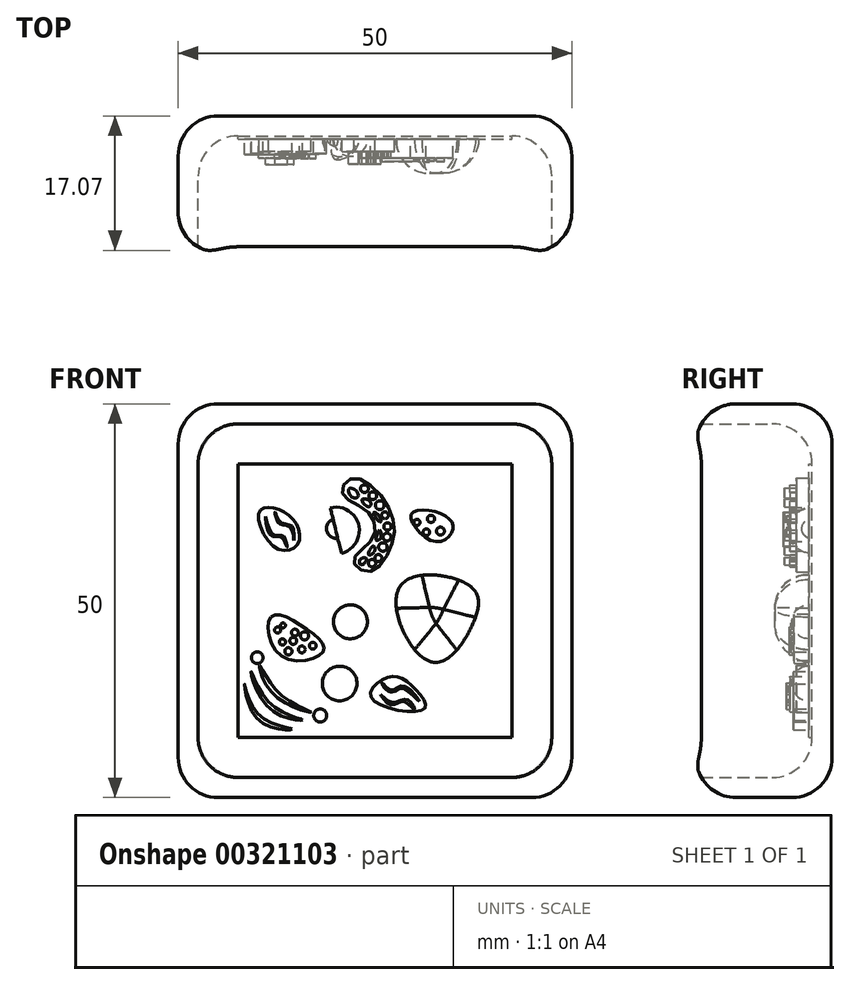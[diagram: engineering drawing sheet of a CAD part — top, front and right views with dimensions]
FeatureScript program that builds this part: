
annotation { "Feature Type Name" : "Feature", "Feature Type Description" : "" }
export const myFeature = defineFeature(function(context is Context, id is Id, definition is map)
    precondition{}
    {
        {
            var Q0;
            Q0=qCreatedBy(makeId("Front.planeOp"),FACE);
            var sketch = newSketch(context, id + "F0", { "sketchPlane" : qUnion([Q0])});
            skLineSegment(sketch, "E0.bottom", {"start": v(0, 0) * mm, "end": v(50, 0) * mm});
            skLineSegment(sketch, "E0.top", {"start": v(0, 50) * mm, "end": v(50, 50) * mm});
            skLineSegment(sketch, "E0.left", {"start": v(0, 0) * mm, "end": v(0, 50) * mm});
            skLineSegment(sketch, "E0.right", {"start": v(50, 0) * mm, "end": v(50, 50) * mm});
            skSolve(sketch);
        }
        {
            var Q0;
            Q0=makeQuery(id+"F0.imprint","IMPRINT",FACE,{"disambiguationData":[TD([[makeQuery(id+"F0.imprint","IMPRINT",EDGE,{"derivedFrom":sQuery(id+"F0.wireOp",EDGE,"E0.bottom")}),1.0]])]});
            var sketch = newSketch(context, id + "F1", { "sketchPlane" : qUnion([Q0])});
            skSolve(sketch);
        }
        {
            var Q0;
            Q0=makeQuery(id+"F1.imprint","IMPRINT",FACE,{"disambiguationData":[TD([[makeQuery(id+"F1.imprint","IMPRINT",EDGE,{"derivedFrom":makeQuery(id+"F0.imprint","IMPRINT",EDGE,{"derivedFrom":sQuery(id+"F0.wireOp",EDGE,"E0.bottom")})}),1.0]])]});
            extrude(context, id + "F2", {"entities" : qUnion([Q0]), "depth" : 17.3 * mm});
        }
        {
            var Q0;
            Q0=makeQuery(id+"F2.opExtrude","CAP_FACE",FACE,{"disambiguationData":[OSD([sQuery(id+"F0.wireOp",EDGE,"E0.bottom"),sQuery(id+"F0.wireOp",EDGE,"E0.top"),sQuery(id+"F0.wireOp",EDGE,"E0.left"),sQuery(id+"F0.wireOp",EDGE,"E0.right")])],"isStart":false});
            shell(context, id + "F3", {"entities" : qUnion([Q0]), "thickness" : 2.54 * mm});
        }
        {
            var Q0;
            Q0=makeQuery(id+"F3.opShell","OFFSET_FACE",FACE,{"disambiguationData":[OSD([sQuery(id+"F0.wireOp",EDGE,"E0.bottom"),sQuery(id+"F0.wireOp",EDGE,"E0.top"),sQuery(id+"F0.wireOp",EDGE,"E0.left"),sQuery(id+"F0.wireOp",EDGE,"E0.right")])]});
            var Q1;
            Q1=makeQuery(id+"F2.opExtrude","SWEPT_EDGE",EDGE,{"disambiguationData":[OSD([sQuery(id+"F0.wireOp",EDGE,"E0.top"),sQuery(id+"F0.wireOp",EDGE,"E0.right")])]});
            var Q2;
            Q2=makeQuery(id+"F2.opExtrude","SWEPT_EDGE",EDGE,{"disambiguationData":[OSD([sQuery(id+"F0.wireOp",EDGE,"E0.top"),sQuery(id+"F0.wireOp",EDGE,"E0.left")])]});
            var Q3;
            Q3=makeQuery(id+"F2.opExtrude","SWEPT_EDGE",EDGE,{"disambiguationData":[OSD([sQuery(id+"F0.wireOp",EDGE,"E0.bottom"),sQuery(id+"F0.wireOp",EDGE,"E0.left")])]});
            var Q4;
            Q4=makeQuery(id+"F2.opExtrude","SWEPT_EDGE",EDGE,{"disambiguationData":[OSD([sQuery(id+"F0.wireOp",EDGE,"E0.bottom"),sQuery(id+"F0.wireOp",EDGE,"E0.right")])]});
            var Q5;
            Q5=makeQuery(id+"F2.opExtrude","CAP_EDGE",EDGE,{"disambiguationData":[OSD([sQuery(id+"F0.wireOp",EDGE,"E0.top")])],"isStart":true});
            var Q6;
            Q6=makeQuery(id+"F2.opExtrude","CAP_EDGE",EDGE,{"disambiguationData":[OSD([sQuery(id+"F0.wireOp",EDGE,"E0.bottom")])],"isStart":true});
            var Q7;
            Q7=makeQuery(id+"F3.opShell","OFFSET_EDGE",EDGE,{"disambiguationData":[OSD([sQuery(id+"F0.wireOp",EDGE,"E0.top"),sQuery(id+"F0.wireOp",EDGE,"E0.right")])]});
            var Q8;
            Q8=makeQuery(id+"F3.opShell","OFFSET_EDGE",EDGE,{"disambiguationData":[OSD([sQuery(id+"F0.wireOp",EDGE,"E0.bottom"),sQuery(id+"F0.wireOp",EDGE,"E0.right")])]});
            var Q9;
            Q9=makeQuery(id+"F3.opShell","OFFSET_EDGE",EDGE,{"disambiguationData":[OSD([sQuery(id+"F0.wireOp",EDGE,"E0.bottom"),sQuery(id+"F0.wireOp",EDGE,"E0.left")])]});
            var Q10;
            Q10=makeQuery(id+"F3.opShell","OFFSET_EDGE",EDGE,{"disambiguationData":[OSD([sQuery(id+"F0.wireOp",EDGE,"E0.top"),sQuery(id+"F0.wireOp",EDGE,"E0.left")])]});
            fillet(context, id + "F4", {"entities" : qUnion([Q0, Q1, Q2, Q3, Q4, Q5, Q6, Q7, Q8, Q9, Q10]), "radius" : 5.08 * mm, "tangentPropagation" : true, "allowEdgeOverflow" : false});
        }
        {
            var Q0;
            Q0=makeQuery(id+"F3.opShell","OFFSET_FACE",FACE,{"disambiguationData":[OSD([sQuery(id+"F0.wireOp",EDGE,"E0.bottom"),sQuery(id+"F0.wireOp",EDGE,"E0.top"),sQuery(id+"F0.wireOp",EDGE,"E0.left"),sQuery(id+"F0.wireOp",EDGE,"E0.right")])]});
            var Q1;
            Q1=makeQuery(id+"F2.opExtrude","CAP_EDGE",EDGE,{"disambiguationData":[OSD([sQuery(id+"F0.wireOp",EDGE,"E0.left")])],"isStart":true});
            var Q2;
            Q2=makeQuery(id+"F2.opExtrude","CAP_EDGE",EDGE,{"disambiguationData":[OSD([sQuery(id+"F0.wireOp",EDGE,"E0.right")])],"isStart":true});
            fillet(context, id + "F5", {"entities" : qUnion([Q0, Q1, Q2]), "radius" : 5.08 * mm, "tangentPropagation" : true, "allowEdgeOverflow" : false});
        }
        {
            var Q0;
            Q0=makeQuery(id+"F2.opExtrude","CAP_EDGE",EDGE,{"disambiguationData":[OSD([sQuery(id+"F0.wireOp",EDGE,"E0.right")])],"isStart":false});
            fillet(context, id + "F6", {"entities" : qUnion([Q0]), "radius" : 5.08 * mm, "tangentPropagation" : true, "allowEdgeOverflow" : false});
        }
        {
            var Q0;
            Q0=makeQuery(id+"F3.opShell","OFFSET_FACE",FACE,{"disambiguationData":[OSD([sQuery(id+"F0.wireOp",EDGE,"E0.bottom"),sQuery(id+"F0.wireOp",EDGE,"E0.top"),sQuery(id+"F0.wireOp",EDGE,"E0.left"),sQuery(id+"F0.wireOp",EDGE,"E0.right")])]});
            var sketch = newSketch(context, id + "F7", { "sketchPlane" : qUnion([Q0])});
            skLineSegment(sketch, "E1", {"start": v(20.1, 35.5) * mm, "end": v(20.1, 32.84) * mm});
            skArc(sketch, "E2", {"start": v(20.1, 32.84) * mm, "mid": v(21.4, 34.17) * mm, "end": v(20.1, 35.5) * mm});
            skSolve(sketch);
        }
        {
            var Q0;
            Q0=makeQuery(id+"F7.imprint","IMPRINT",FACE,{"disambiguationData":[TD([[makeQuery(id+"F7.imprint","IMPRINT",EDGE,{"derivedFrom":sQuery(id+"F7.wireOp",EDGE,"E1")}),1.0]])]});
            var Q1;
            Q1=sQuery(id+"F7.wireOp",EDGE,"E1");
            revolve(context, id + "F8", {"entities" : qUnion([Q0]), "axis" : qUnion([Q1]), "revolveType" : RevolveType.ONE_DIRECTION, "angle" : 180 * degree});
        }
        {
            var Q0;
            Q0=makeQuery(id+"F3.opShell","OFFSET_FACE",FACE,{"disambiguationData":[OSD([sQuery(id+"F0.wireOp",EDGE,"E0.bottom"),sQuery(id+"F0.wireOp",EDGE,"E0.top"),sQuery(id+"F0.wireOp",EDGE,"E0.left"),sQuery(id+"F0.wireOp",EDGE,"E0.right")])]});
            var sketch = newSketch(context, id + "F9", { "sketchPlane" : qUnion([Q0])});
            skLineSegment(sketch, "E3", {"start": v(19.32, 36.82) * mm, "end": v(20.75, 31) * mm});
            skArc(sketch, "E4", {"start": v(20.75, 31) * mm, "mid": v(22.96, 34.64) * mm, "end": v(19.32, 36.82) * mm});
            skSolve(sketch);
        }
        {
            var Q0;
            Q0=makeQuery(id+"F9.imprint","IMPRINT",FACE,{"disambiguationData":[TD([[makeQuery(id+"F9.imprint","IMPRINT",EDGE,{"derivedFrom":sQuery(id+"F9.wireOp",EDGE,"E3")}),1.0]])]});
            var Q1;
            Q1=sQuery(id+"F9.wireOp",EDGE,"E3");
            revolve(context, id + "F10", {"entities" : qUnion([Q0]), "axis" : qUnion([Q1]), "revolveType" : RevolveType.ONE_DIRECTION, "angle" : 90 * degree});
        }
        {
            var Q0;
            Q0=makeQuery(id+"F3.opShell","OFFSET_FACE",FACE,{"disambiguationData":[OSD([sQuery(id+"F0.wireOp",EDGE,"E0.bottom"),sQuery(id+"F0.wireOp",EDGE,"E0.top"),sQuery(id+"F0.wireOp",EDGE,"E0.left"),sQuery(id+"F0.wireOp",EDGE,"E0.right")])]});
            var sketch = newSketch(context, id + "F11", { "sketchPlane" : qUnion([Q0])});
            skFitSpline(sketch, "E5", {"points": [v(37, 26.9) * mm, v(37.56, 22.37) * mm, v(32.09, 17.25) * mm, v(28.13, 26.72) * mm, v(37, 26.9) * mm]});
            skSolve(sketch);
        }
        {
            var Q0;
            Q0=makeQuery(id+"F11.imprint","IMPRINT",FACE,{"disambiguationData":[TD([[makeQuery(id+"F11.imprint","IMPRINT",EDGE,{"derivedFrom":sQuery(id+"F11.wireOp",EDGE,"E5")}),-1.0]])]});
            extrude(context, id + "F12", {"entities" : qUnion([Q0]), "depth" : 4.73 * mm});
        }
        {
            var Q0;
            Q0=makeQuery(id+"F3.opShell","OFFSET_FACE",FACE,{"disambiguationData":[OSD([sQuery(id+"F0.wireOp",EDGE,"E0.bottom"),sQuery(id+"F0.wireOp",EDGE,"E0.top"),sQuery(id+"F0.wireOp",EDGE,"E0.left"),sQuery(id+"F0.wireOp",EDGE,"E0.right")])]});
            var sketch = newSketch(context, id + "F13", { "sketchPlane" : qUnion([Q0])});
            skFitSpline(sketch, "E6", {"points": [v(11.8, 22.95) * mm, v(16.02, 21.6) * mm, v(18.48, 18.58) * mm, v(13.15, 17.95) * mm, v(11.8, 22.95) * mm]});
            skSolve(sketch);
        }
        {
            var Q0;
            Q0 = qSketchRegion(id + "F13", true);
            extrude(context, id + "F14", {"entities" : qUnion([Q0]), "operationType" : NewBodyOperationType.ADD, "depth" : 2.28 * mm});
        }
        {
            var Q0;
            Q0=makeQuery(id+"F14.opExtrude","CAP_FACE",FACE,{"disambiguationData":[OSD([sQuery(id+"F13.wireOp",EDGE,"E6")])],"isStart":false});
            var sketch = newSketch(context, id + "F15", { "sketchPlane" : qUnion([Q0])});
            skCircle(sketch, "E7", {"center": v(15.71, 18.8) * mm, "radius": 0.44 * mm});
            skSolve(sketch);
        }
        {
            var Q0;
            Q0 = qSketchRegion(id + "F15", true);
            extrude(context, id + "F16", {"entities" : qUnion([Q0]), "operationType" : NewBodyOperationType.ADD, "depth" : 0.35 * mm});
        }
        {
            var Q0;
            Q0=makeQuery(id+"F14.opExtrude","CAP_FACE",FACE,{"disambiguationData":[OSD([sQuery(id+"F13.wireOp",EDGE,"E6")])],"isStart":false});
            var sketch = newSketch(context, id + "F17", { "sketchPlane" : qUnion([Q0])});
            skCircle(sketch, "E8", {"center": v(13.24, 19.75) * mm, "radius": 0.4 * mm});
            skSolve(sketch);
        }
        {
            var Q0;
            Q0 = qSketchRegion(id + "F17", true);
            extrude(context, id + "F18", {"entities" : qUnion([Q0]), "operationType" : NewBodyOperationType.ADD, "depth" : 0.35 * mm});
        }
        {
            var Q0;
            Q0=makeQuery(id+"F14.opExtrude","CAP_FACE",FACE,{"disambiguationData":[OSD([sQuery(id+"F13.wireOp",EDGE,"E6")])],"isStart":false});
            var sketch = newSketch(context, id + "F19", { "sketchPlane" : qUnion([Q0])});
            skCircle(sketch, "E9", {"center": v(13.32, 21.86) * mm, "radius": 0.3 * mm});
            skSolve(sketch);
        }
        {
            var Q0;
            Q0 = qSketchRegion(id + "F19", true);
            extrude(context, id + "F20", {"entities" : qUnion([Q0]), "operationType" : NewBodyOperationType.ADD, "depth" : 0.39 * mm});
        }
        {
            var Q0;
            Q0=makeQuery(id+"F14.opExtrude","CAP_FACE",FACE,{"disambiguationData":[OSD([sQuery(id+"F13.wireOp",EDGE,"E6")])],"isStart":false});
            var sketch = newSketch(context, id + "F21", { "sketchPlane" : qUnion([Q0])});
            skCircle(sketch, "E10", {"center": v(14.84, 20.95) * mm, "radius": 0.43 * mm});
            skSolve(sketch);
        }
        {
            var Q0;
            Q0 = qSketchRegion(id + "F21", true);
            var Q1;
            Q1=makeQuery(id+"F3.opShell","OFFSET_FACE",FACE,{"disambiguationData":[OSD([sQuery(id+"F0.wireOp",EDGE,"E0.bottom"),sQuery(id+"F0.wireOp",EDGE,"E0.top"),sQuery(id+"F0.wireOp",EDGE,"E0.left"),sQuery(id+"F0.wireOp",EDGE,"E0.right")])]});
            extrude(context, id + "F22", {"entities" : qUnion([Q0, Q1]), "operationType" : NewBodyOperationType.ADD, "depth" : 0.4 * mm});
        }
        {
            var Q0;
            Q0=makeQuery(id+"F14.opExtrude","CAP_FACE",FACE,{"disambiguationData":[OSD([sQuery(id+"F13.wireOp",EDGE,"E6")])],"isStart":false});
            var sketch = newSketch(context, id + "F23", { "sketchPlane" : qUnion([Q0])});
            skSolve(sketch);
        }
        {
            var Q0;
            Q0=makeQuery(id+"F23.imprint","IMPRINT",FACE,{"disambiguationData":[TD([[makeQuery(id+"F23.imprint","IMPRINT",EDGE,{"derivedFrom":makeQuery(id+"F14.opExtrude","CAP_EDGE",EDGE,{"disambiguationData":[OSD([sQuery(id+"F13.wireOp",EDGE,"E6")])],"isStart":false})}),-1.0]])]});
            var sketch = newSketch(context, id + "F24", { "sketchPlane" : qUnion([Q0])});
            skSolve(sketch);
        }
        {
            var Q0;
            Q0=makeQuery(id+"F22.opExtrude","CAP_FACE",FACE,{"disambiguationData":[OSD([sQuery(id+"F0.wireOp",EDGE,"E0.bottom"),sQuery(id+"F0.wireOp",EDGE,"E0.top"),sQuery(id+"F0.wireOp",EDGE,"E0.left"),sQuery(id+"F0.wireOp",EDGE,"E0.right")])],"isStart":false});
            var sketch = newSketch(context, id + "F25", { "sketchPlane" : qUnion([Q0])});
            skFitSpline(sketch, "E11", {"points": [v(29.59, 35.96) * mm, v(33.47, 36.03) * mm, v(34.91, 34.05) * mm, v(32.52, 32.54) * mm, v(29.59, 35.96) * mm]});
            skSolve(sketch);
        }
        {
            var Q0;
            Q0 = qSketchRegion(id + "F25", true);
            extrude(context, id + "F26", {"entities" : qUnion([Q0]), "operationType" : NewBodyOperationType.ADD, "depth" : 2.37 * mm});
        }
        {
            var Q0;
            Q0=makeQuery(id+"F26.opExtrude","CAP_FACE",FACE,{"disambiguationData":[OSD([sQuery(id+"F25.wireOp",EDGE,"E11")])],"isStart":false});
            var sketch = newSketch(context, id + "F27", { "sketchPlane" : qUnion([Q0])});
            skCircle(sketch, "E12", {"center": v(33.32, 33.84) * mm, "radius": 0.5 * mm});
            skSolve(sketch);
        }
        {
            var Q0;
            Q0 = qSketchRegion(id + "F27", true);
            extrude(context, id + "F28", {"entities" : qUnion([Q0]), "operationType" : NewBodyOperationType.ADD, "depth" : 0.45 * mm});
        }
        {
            var Q0;
            Q0=makeQuery(id+"F26.opExtrude","CAP_FACE",FACE,{"disambiguationData":[OSD([sQuery(id+"F25.wireOp",EDGE,"E11")])],"isStart":false});
            var sketch = newSketch(context, id + "F29", { "sketchPlane" : qUnion([Q0])});
            skCircle(sketch, "E13", {"center": v(32.12, 35.4) * mm, "radius": 0.46 * mm});
            skSolve(sketch);
        }
        {
            var Q0;
            Q0 = qSketchRegion(id + "F29", true);
            extrude(context, id + "F30", {"entities" : qUnion([Q0]), "operationType" : NewBodyOperationType.ADD, "depth" : 0.42 * mm});
        }
        {
            var Q0;
            Q0=makeQuery(id+"F26.opExtrude","CAP_FACE",FACE,{"disambiguationData":[OSD([sQuery(id+"F25.wireOp",EDGE,"E11")])],"isStart":false});
            var sketch = newSketch(context, id + "F31", { "sketchPlane" : qUnion([Q0])});
            skCircle(sketch, "E14", {"center": v(30.33, 34.94) * mm, "radius": 0.4 * mm});
            skSolve(sketch);
        }
        {
            var Q0;
            Q0 = qSketchRegion(id + "F31", true);
            extrude(context, id + "F32", {"entities" : qUnion([Q0]), "operationType" : NewBodyOperationType.ADD, "depth" : 0.3 * mm});
        }
        {
            var Q0;
            Q0=makeQuery(id+"F22.opExtrude","CAP_FACE",FACE,{"disambiguationData":[OSD([sQuery(id+"F0.wireOp",EDGE,"E0.bottom"),sQuery(id+"F0.wireOp",EDGE,"E0.top"),sQuery(id+"F0.wireOp",EDGE,"E0.left"),sQuery(id+"F0.wireOp",EDGE,"E0.right")])],"isStart":false});
            var sketch = newSketch(context, id + "F33", { "sketchPlane" : qUnion([Q0])});
            skFitSpline(sketch, "E15", {"points": [v(26.58, 15.26) * mm, v(29.8, 14.11) * mm, v(31.24, 11.22) * mm, v(24.55, 12.68) * mm, v(26.58, 15.26) * mm]});
            skFitSpline(sketch, "E16", {"points": [v(12.15, 36.78) * mm, v(14.97, 34.86) * mm, v(15.1, 32.04) * mm, v(12.4, 31.72) * mm, v(10.26, 36.2) * mm, v(12.15, 36.78) * mm]});
            skSolve(sketch);
        }
        {
            var Q0;
            Q0=makeQuery(id+"F33.imprint","IMPRINT",FACE,{"disambiguationData":[TD([[makeQuery(id+"F33.imprint","IMPRINT",EDGE,{"derivedFrom":sQuery(id+"F33.wireOp",EDGE,"E16")}),-1.0]])]});
            var Q1;
            Q1=makeQuery(id+"F33.imprint","IMPRINT",FACE,{"disambiguationData":[TD([[makeQuery(id+"F33.imprint","IMPRINT",EDGE,{"derivedFrom":sQuery(id+"F33.wireOp",EDGE,"E15")}),-1.0]])]});
            extrude(context, id + "F34", {"entities" : qUnion([Q0, Q1]), "depth" : 2.38 * mm});
        }
        {
            var Q0;
            Q0=makeQuery(id+"F34.opExtrude","CAP_FACE",FACE,{"disambiguationData":[OSD([sQuery(id+"F33.wireOp",EDGE,"E15")])],"isStart":false});
            var sketch = newSketch(context, id + "F35", { "sketchPlane" : qUnion([Q0])});
            skFitSpline(sketch, "E17", {"points": [v(30.65, 12.2) * mm, v(28.67, 14.17) * mm, v(27.02, 13.66) * mm, v(25.92, 14.56) * mm, v(26.32, 13.81) * mm, v(27.45, 13.44) * mm, v(28.5, 13.88) * mm, v(30.65, 12.2) * mm]});
            skFitSpline(sketch, "E18", {"points": [v(25.7, 13.08) * mm, v(26.97, 11.8) * mm, v(28.71, 12.19) * mm, v(30.03, 11.17) * mm, v(29.21, 12.42) * mm, v(27.06, 12.12) * mm, v(25.7, 13.08) * mm]});
            skSolve(sketch);
        }
        {
            var Q0;
            Q0 = qSketchRegion(id + "F35", true);
            extrude(context, id + "F36", {"entities" : qUnion([Q0]), "operationType" : NewBodyOperationType.ADD, "depth" : 0.47 * mm});
        }
        {
            var Q0;
            Q0=makeQuery(id+"F34.opExtrude","CAP_FACE",FACE,{"disambiguationData":[OSD([sQuery(id+"F33.wireOp",EDGE,"E16")])],"isStart":false});
            var sketch = newSketch(context, id + "F37", { "sketchPlane" : qUnion([Q0])});
            skFitSpline(sketch, "E19", {"points": [v(11.11, 35.7) * mm, v(11.7, 33.36) * mm, v(13.12, 33.05) * mm, v(13.86, 31.8) * mm, v(13.7, 32.52) * mm, v(13.2, 33.24) * mm, v(11.88, 33.6) * mm, v(11.11, 35.7) * mm]});
            skFitSpline(sketch, "E20", {"points": [v(14.7, 32.66) * mm, v(14.53, 34.36) * mm, v(13.05, 34.95) * mm, v(12.3, 36.27) * mm, v(12.46, 35.51) * mm, v(12.91, 34.73) * mm, v(14.35, 34.18) * mm, v(14.7, 32.66) * mm]});
            skSolve(sketch);
        }
        {
            var Q0;
            Q0 = qSketchRegion(id + "F37", true);
            extrude(context, id + "F38", {"entities" : qUnion([Q0]), "operationType" : NewBodyOperationType.ADD, "depth" : 0.87 * mm});
        }
        {
            var Q0;
            Q0=makeQuery(id+"F12.opExtrude","CAP_EDGE",EDGE,{"disambiguationData":[OSD([sQuery(id+"F11.wireOp",EDGE,"E5")])],"isStart":false});
            fillet(context, id + "F39", {"entities" : qUnion([Q0]), "radius" : 4.14 * mm, "tangentPropagation" : true, "allowEdgeOverflow" : false});
        }
        {
            var Q0;
            Q0=makeQuery(id+"F22.opExtrude","CAP_FACE",FACE,{"disambiguationData":[OSD([sQuery(id+"F0.wireOp",EDGE,"E0.bottom"),sQuery(id+"F0.wireOp",EDGE,"E0.top"),sQuery(id+"F0.wireOp",EDGE,"E0.left"),sQuery(id+"F0.wireOp",EDGE,"E0.right")])],"isStart":false});
            var sketch = newSketch(context, id + "F40", { "sketchPlane" : qUnion([Q0])});
            skLineSegment(sketch, "E21", {"start": v(23.9, 21.55) * mm, "end": v(19.88, 23.09) * mm});
            skArc(sketch, "E22", {"start": v(23.9, 21.55) * mm, "mid": v(22.66, 24.33) * mm, "end": v(19.88, 23.09) * mm});
            skSolve(sketch);
        }
        {
            var Q0;
            Q0=makeQuery(id+"F40.imprint","IMPRINT",FACE,{"disambiguationData":[TD([[makeQuery(id+"F40.imprint","IMPRINT",EDGE,{"derivedFrom":sQuery(id+"F40.wireOp",EDGE,"E21")}),-1.0]])]});
            var Q1;
            Q1=sQuery(id+"F40.wireOp",EDGE,"E21");
            revolve(context, id + "F41", {"entities" : qUnion([Q0]), "axis" : qUnion([Q1]), "revolveType" : RevolveType.ONE_DIRECTION, "oppositeDirection" : true, "angle" : 180 * degree});
        }
        {
            var Q0;
            Q0=makeQuery(id+"F22.opExtrude","CAP_FACE",FACE,{"disambiguationData":[OSD([sQuery(id+"F0.wireOp",EDGE,"E0.bottom"),sQuery(id+"F0.wireOp",EDGE,"E0.top"),sQuery(id+"F0.wireOp",EDGE,"E0.left"),sQuery(id+"F0.wireOp",EDGE,"E0.right")])],"isStart":false});
            var sketch = newSketch(context, id + "F42", { "sketchPlane" : qUnion([Q0])});
            skLineSegment(sketch, "E23", {"start": v(22.37, 15.7) * mm, "end": v(18.67, 13.25) * mm});
            skArc(sketch, "E24", {"start": v(18.67, 13.25) * mm, "mid": v(21.73, 12.65) * mm, "end": v(22.37, 15.7) * mm});
            skSolve(sketch);
        }
        {
            var Q0;
            Q0=makeQuery(id+"F42.imprint","IMPRINT",FACE,{"disambiguationData":[TD([[makeQuery(id+"F42.imprint","IMPRINT",EDGE,{"derivedFrom":sQuery(id+"F42.wireOp",EDGE,"E23")}),1.0]])]});
            var Q1;
            Q1=sQuery(id+"F42.wireOp",EDGE,"E23");
            revolve(context, id + "F43", {"entities" : qUnion([Q0]), "axis" : qUnion([Q1]), "revolveType" : RevolveType.ONE_DIRECTION, "angle" : 180 * degree});
        }
        {
            var Q0;
            Q0=makeQuery(id+"F22.opExtrude","CAP_FACE",FACE,{"disambiguationData":[OSD([sQuery(id+"F0.wireOp",EDGE,"E0.bottom"),sQuery(id+"F0.wireOp",EDGE,"E0.top"),sQuery(id+"F0.wireOp",EDGE,"E0.left"),sQuery(id+"F0.wireOp",EDGE,"E0.right")])],"isStart":false});
            var sketch = newSketch(context, id + "F44", { "sketchPlane" : qUnion([Q0])});
            skFitSpline(sketch, "E25", {"points": [v(10.33, 16.78) * mm, v(12.23, 13) * mm, v(16.88, 10.83) * mm, v(12.93, 13.17) * mm, v(10.33, 16.78) * mm]});
            skSolve(sketch);
        }
        {
            var Q0;
            Q0 = qSketchRegion(id + "F44", true);
            extrude(context, id + "F45", {"entities" : qUnion([Q0]), "depth" : 1.55 * mm});
        }
        {
            var Q0;
            Q0=makeQuery(id+"F22.opExtrude","CAP_FACE",FACE,{"disambiguationData":[OSD([sQuery(id+"F0.wireOp",EDGE,"E0.bottom"),sQuery(id+"F0.wireOp",EDGE,"E0.top"),sQuery(id+"F0.wireOp",EDGE,"E0.left"),sQuery(id+"F0.wireOp",EDGE,"E0.right")])],"isStart":false});
            var sketch = newSketch(context, id + "F46", { "sketchPlane" : qUnion([Q0])});
            skFitSpline(sketch, "E26", {"points": [v(15.8, 9.85) * mm, v(11.61, 11.28) * mm, v(9.24, 16.03) * mm, v(11.78, 11.87) * mm, v(15.8, 9.85) * mm]});
            skFitSpline(sketch, "E27", {"points": [v(14.47, 8.68) * mm, v(10.27, 9.8) * mm, v(8.43, 14.42) * mm, v(10.27, 10.5) * mm, v(14.47, 8.68) * mm]});
            skSolve(sketch);
        }
        {
            var Q0;
            Q0 = qSketchRegion(id + "F46", true);
            extrude(context, id + "F47", {"entities" : qUnion([Q0]), "depth" : 1.97 * mm});
        }
        {
            var Q0;
            Q0=makeQuery(id+"F22.opExtrude","CAP_FACE",FACE,{"disambiguationData":[OSD([sQuery(id+"F0.wireOp",EDGE,"E0.bottom"),sQuery(id+"F0.wireOp",EDGE,"E0.top"),sQuery(id+"F0.wireOp",EDGE,"E0.left"),sQuery(id+"F0.wireOp",EDGE,"E0.right")])],"isStart":false});
            var sketch = newSketch(context, id + "F48", { "sketchPlane" : qUnion([Q0])});
            skFitSpline(sketch, "E28", {"points": [v(20.88, 38.62) * mm, v(24.15, 36.24) * mm, v(24.65, 32.82) * mm, v(22.31, 30.13) * mm, v(24.14, 28.68) * mm, v(27.18, 32.2) * mm, v(26.47, 37.31) * mm, v(22.15, 40.56) * mm, v(20.88, 38.62) * mm]});
            skSolve(sketch);
        }
        {
            var Q0;
            Q0 = qSketchRegion(id + "F48", true);
            extrude(context, id + "F49", {"entities" : qUnion([Q0]), "depth" : 1.6 * mm});
        }
        {
            var Q0;
            Q0=makeQuery(id+"F49.opExtrude","CAP_FACE",FACE,{"disambiguationData":[OSD([sQuery(id+"F48.wireOp",EDGE,"E28")])],"isStart":false});
            var sketch = newSketch(context, id + "F50", { "sketchPlane" : qUnion([Q0])});
            skFitSpline(sketch, "E29", {"points": [v(21.7, 39.19) * mm, v(22.52, 39.05) * mm, v(22.85, 38.22) * mm, v(22.13, 38.13) * mm, v(21.7, 39.19) * mm]});
            skFitSpline(sketch, "E30", {"points": [v(23.39, 37.84) * mm, v(24.1, 37.8) * mm, v(24.49, 37.2) * mm, v(24.05, 36.95) * mm, v(23.39, 37.84) * mm]});
            skFitSpline(sketch, "E31", {"points": [v(24.83, 36.17) * mm, v(25.47, 35.86) * mm, v(25.68, 35) * mm, v(24.83, 36.17) * mm]});
            skFitSpline(sketch, "E32", {"points": [v(25.6, 33.96) * mm, v(25.8, 33.34) * mm, v(25.62, 32.81) * mm, v(25.15, 32.69) * mm, v(25.28, 33.33) * mm, v(25.6, 33.96) * mm]});
            skFitSpline(sketch, "E33", {"points": [v(24.83, 31.95) * mm, v(24.27, 31.32) * mm, v(24.25, 30.8) * mm, v(24.8, 31.07) * mm, v(25, 31.54) * mm, v(24.83, 31.95) * mm]});
            skFitSpline(sketch, "E34", {"points": [v(23.9, 30.35) * mm, v(23.25, 30.35) * mm, v(23.07, 29.65) * mm, v(23.57, 29.68) * mm, v(23.9, 30.35) * mm]});
            skSolve(sketch);
        }
        {
            var Q0;
            Q0 = qSketchRegion(id + "F50", true);
            extrude(context, id + "F51", {"entities" : qUnion([Q0]), "depth" : 1.53 * mm});
        }
        {
            var Q0;
            Q0=makeQuery(id+"F49.opExtrude","CAP_FACE",FACE,{"disambiguationData":[OSD([sQuery(id+"F48.wireOp",EDGE,"E28")])],"isStart":false});
            var sketch = newSketch(context, id + "F52", { "sketchPlane" : qUnion([Q0])});
            skCircle(sketch, "E35", {"center": v(23.67, 39.23) * mm, "radius": 0.5 * mm});
            skCircle(sketch, "E36", {"center": v(25.62, 37.13) * mm, "radius": 0.57 * mm});
            skCircle(sketch, "E37", {"center": v(26.6, 34.42) * mm, "radius": 0.47 * mm});
            skCircle(sketch, "E38", {"center": v(26.01, 31.82) * mm, "radius": 0.54 * mm});
            skCircle(sketch, "E39", {"center": v(24.64, 29.77) * mm, "radius": 0.47 * mm});
            skSolve(sketch);
        }
        {
            var Q0;
            Q0 = qSketchRegion(id + "F52", true);
            extrude(context, id + "F53", {"entities" : qUnion([Q0]), "depth" : 0.83 * mm});
        }
        {
            var Q0;
            Q0=makeQuery(id+"F22.opExtrude","CAP_FACE",FACE,{"disambiguationData":[OSD([sQuery(id+"F0.wireOp",EDGE,"E0.bottom"),sQuery(id+"F0.wireOp",EDGE,"E0.top"),sQuery(id+"F0.wireOp",EDGE,"E0.left"),sQuery(id+"F0.wireOp",EDGE,"E0.right")])],"isStart":false});
            var sketch = newSketch(context, id + "F54", { "sketchPlane" : qUnion([Q0])});
            skCircle(sketch, "E40", {"center": v(18.05, 10.41) * mm, "radius": 0.83 * mm});
            skCircle(sketch, "E41", {"center": v(10.05, 17.76) * mm, "radius": 0.74 * mm});
            skSolve(sketch);
        }
        {
            var Q0;
            Q0 = qSketchRegion(id + "F54", true);
            extrude(context, id + "F55", {"entities" : qUnion([Q0]), "depth" : 1.83 * mm});
        }
        {
            var Q0;
            Q0=makeQuery(id+"F49.opExtrude","CAP_FACE",FACE,{"disambiguationData":[OSD([sQuery(id+"F48.wireOp",EDGE,"E28")])],"isStart":false});
            var sketch = newSketch(context, id + "F56", { "sketchPlane" : qUnion([Q0])});
            skCircle(sketch, "E42", {"center": v(24.72, 38.33) * mm, "radius": 0.5 * mm});
            skCircle(sketch, "E43", {"center": v(26.28, 35.84) * mm, "radius": 0.43 * mm});
            skCircle(sketch, "E44", {"center": v(26.53, 33.07) * mm, "radius": 0.5 * mm});
            skCircle(sketch, "E45", {"center": v(25.44, 30.42) * mm, "radius": 0.45 * mm});
            skSolve(sketch);
        }
        {
            var Q0;
            Q0 = qSketchRegion(id + "F56", true);
            extrude(context, id + "F57", {"entities" : qUnion([Q0]), "depth" : 0.75 * mm});
        }
        {
            var Q0;
            Q0=makeQuery(id+"F26.opExtrude","CAP_FACE",FACE,{"disambiguationData":[OSD([sQuery(id+"F25.wireOp",EDGE,"E11")])],"isStart":false});
            var sketch = newSketch(context, id + "F58", { "sketchPlane" : qUnion([Q0])});
            skSolve(sketch);
        }
        {
            var Q0;
            Q0=makeQuery(id+"F58.imprint","IMPRINT",FACE,{"disambiguationData":[TD([[makeQuery(id+"F58.imprint","IMPRINT",EDGE,{"derivedFrom":makeQuery(id+"F26.opExtrude","CAP_EDGE",EDGE,{"disambiguationData":[OSD([sQuery(id+"F25.wireOp",EDGE,"E11")])],"isStart":false})}),-1.0]])]});
            var sketch = newSketch(context, id + "F59", { "sketchPlane" : qUnion([Q0])});
            skCircle(sketch, "E46", {"center": v(31.53, 33.7) * mm, "radius": 0.42 * mm});
            skSolve(sketch);
        }
        {
            var Q0;
            Q0 = qSketchRegion(id + "F59", true);
            extrude(context, id + "F60", {"entities" : qUnion([Q0]), "operationType" : NewBodyOperationType.ADD, "depth" : 0.55 * mm});
        }
        {
            var Q0;
            Q0=makeQuery(id+"F24.imprint","IMPRINT",FACE,{"disambiguationData":[TD([[makeQuery(id+"F24.imprint","IMPRINT",EDGE,{"derivedFrom":makeQuery(id+"F23.imprint","IMPRINT",EDGE,{"derivedFrom":makeQuery(id+"F14.opExtrude","CAP_EDGE",EDGE,{"disambiguationData":[OSD([sQuery(id+"F13.wireOp",EDGE,"E6")])],"isStart":false})})}),-1.0]])]});
            var sketch = newSketch(context, id + "F61", { "sketchPlane" : qUnion([Q0])});
            skCircle(sketch, "E47", {"center": v(17.1, 19.27) * mm, "radius": 0.43 * mm});
            skCircle(sketch, "E48", {"center": v(14, 18.58) * mm, "radius": 0.46 * mm});
            skCircle(sketch, "E49", {"center": v(12.65, 21.27) * mm, "radius": 0.38 * mm});
            skCircle(sketch, "E50", {"center": v(16.06, 20.53) * mm, "radius": 0.53 * mm});
            skCircle(sketch, "E51", {"center": v(14.62, 19.9) * mm, "radius": 0.44 * mm});
            skSolve(sketch);
        }
        {
            var Q0;
            Q0 = qSketchRegion(id + "F61", true);
            extrude(context, id + "F62", {"entities" : qUnion([Q0]), "operationType" : NewBodyOperationType.ADD, "depth" : 0.57 * mm});
        }
    });
